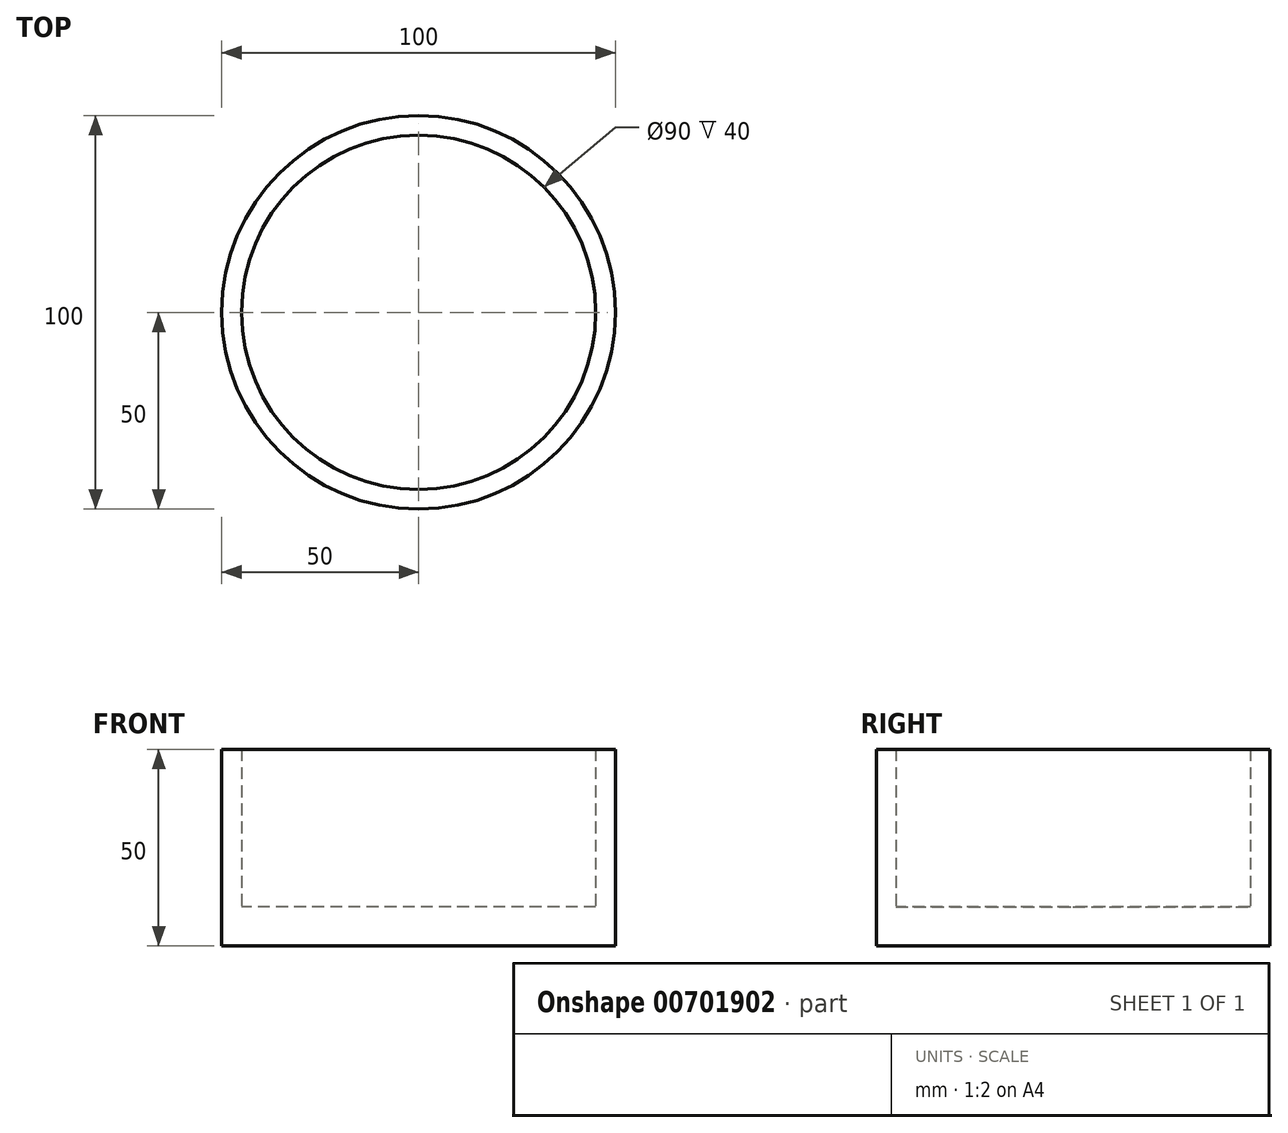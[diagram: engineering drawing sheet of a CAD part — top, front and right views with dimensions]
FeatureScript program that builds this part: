
annotation { "Feature Type Name" : "Feature", "Feature Type Description" : "" }
export const myFeature = defineFeature(function(context is Context, id is Id, definition is map)
    precondition{}
    {
        {
            var Q0;
            Q0=qCreatedBy(makeId("Top.planeOp"),FACE);
            var sketch = newSketch(context, id + "F0", { "sketchPlane" : qUnion([Q0])});
            skCircle(sketch, "E0", {"center": v(0, 0) * mm, "radius": 50 * mm});
            skSolve(sketch);
        }
        {
            var Q0;
            Q0=makeQuery(id+"F0.imprint","IMPRINT",FACE,{"disambiguationData":[TD([[makeQuery(id+"F0.imprint","IMPRINT",EDGE,{"derivedFrom":sQuery(id+"F0.wireOp",EDGE,"E0")}),1.0]])]});
            extrude(context, id + "F1", {"entities" : qUnion([Q0]), "depth" : 10 * mm, "offsetDistance" : 25 * mm});
        }
        {
            var Q0;
            Q0=makeQuery(id+"F1.opExtrude","CAP_FACE",FACE,{"disambiguationData":[OSD([sQuery(id+"F0.wireOp",EDGE,"E0")])],"isStart":false});
            var sketch = newSketch(context, id + "F2", { "sketchPlane" : qUnion([Q0])});
            skCircle(sketch, "E1", {"center": v(0, 0) * mm, "radius": 45 * mm});
            skSolve(sketch);
        }
        {
            var Q0;
            Q0=makeQuery(id+"F2.imprint","IMPRINT",FACE,{"disambiguationData":[TD([[makeQuery(id+"F2.imprint","IMPRINT",EDGE,{"derivedFrom":sQuery(id+"F2.wireOp",EDGE,"E1")}),-1.0]])]});
            extrude(context, id + "F3", {"entities" : qUnion([Q0]), "operationType" : NewBodyOperationType.ADD, "depth" : 40 * mm, "offsetDistance" : 25 * mm});
        }
        {
            var Q0;
            Q0=qCreatedBy(makeId("Right.planeOp"),FACE);
            cPlane(context, id + "F4", {"entities" : qUnion([Q0]), "cplaneType" : CPlaneType.OFFSET, "offset" : 50 * mm, "width" : 150 * mm, "height" : 150 * mm});
        }
    });
